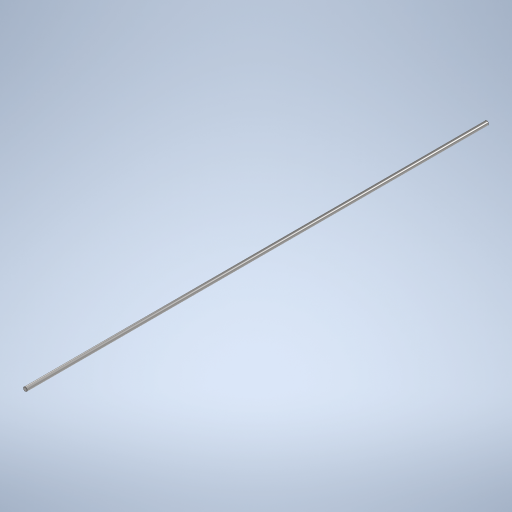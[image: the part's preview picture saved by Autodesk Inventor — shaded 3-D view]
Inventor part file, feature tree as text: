
AUTODESK INVENTOR PART (.ipt)
format: ipt  version: 2023 (Build 270158000, 158)  size: 265,216 bytes
history: native  units: in
note: dims shown in document units (in); Inventor stores cm internally (conversion verified against a paired STEP export)
features: extrude x1, chamfer x1, sketch x1
ambient origin geometry x8: Origin, YZ Plane, XZ Plane, XY Plane, X Axis, Y Axis, Z Axis, Center Point
bodies: Solid1 (feature_tree)
feature tree (3):
  extrude  "Extrusion1"  Depth=36.0in TaperAngle=0.0deg
  chamfer  "Chamfer1"  Distance=0.02in Angle=45.0deg
  sketch  "Sketch1"  dims[d0=0.315in d1=36.0in d2=0.0in d3=0.02in d4=0.125in d5=45.0deg]
